# Revit family: QF_ELECTROLUXPROFESSIONAL_600673_EPBC1W2
name_source: partatom
category: Specialty Equipment
revit_build: Autodesk Revit 2018 (Build: 20190510_1515(x64)
units: mm (PartAtom-declared; Revit-internal decimal feet)

## family parameters
Always vertical = Yes
Cut with Voids When Loaded = No
Part Type = Normal
Room Calculation Point = No
Round Connector Dimension = Use Diameter
Shared = No
Work Plane-Based = No

## types (1)
- QF_ELECTROLUXPROFESSIONAL_600673_EPBC1W2
    Accessory = Yes
    Apparent Power = 0 VA
    Cold Water Connection Height = 126 mm
    Cold Water Flow = 0 GPM
    Cold Water Maximum Pressure = 0.00 psi
    Cold Water Minimum Pressure = 0.00 psi
    Cold Water RI Height = 0 mm  [stored 0 ft]
    Cold Water Size = 1"
    Cold Water Temperature Recommended = 0 °F
    Compressed Air Pressure = 0.00 psi
    Compressed Air Size = 0"
    Compressed Air Volume = 0 GPM
    Condensate Return Size = 0"
    Conn Conduit = Yes
    Cycle = 50 Hz
    Depth = 482 mm
    Depth Actual = 486 mm
    Description = PB WARMER SHUTTLE BREWER, SINGLE
    Direct Waste Size = 0"
    Elec Conn Connection Height = 0 mm  [stored 0 ft]
    Elec Conn RI Height = 227 mm
    FL Amps = 0 A
    Foodservice Equipment Identifier = Yes
    Gas Input Pressure = 0.0
    Gas KW = 0
    Gas Size = 0"
    HP = 3.8 HP
    Height = 761 mm
    Height Actual = 852 mm
    Hot Water Size = 0"
    Identify Quantity as Lot = Yes
    Item Number = 600673
    Length Actual = 232 mm  [stored 0.761155 ft]
    Manufacturer = Electrolux
    Max Overcurrent Protection = 0 A
    Min Ckt Ampacity = 0 A
    Model = EPBC1W2
    Number of Poles = 1
    Phase = 1
    Refrigerant Compressor Remote = Yes
    Refrigeration Liquid Line Size = 0"
    Refrigeration Suction Line Size = 0"
    Steam Pounds per Hour = 0
    Steam Supply Maximum Pressure = 0.00 psi
    Steam Supply Minimum Pressure = 0.00 psi
    Steam Supply Size = 0"
    URL = http://professional.electrolux.com
    URL Manufacturer = http://professional.electrolux.com
    Volts = 230 V
    Watts = 0 W
    Weight = 0.00 lbm
    Weight in Kilograms = 18
    Width = 229 mm

note: source unit labels omitted for Gas Input Pressure — the stored unit's dimension contradicts the parameter name (converter mislabeling)

note: [stored X ft] marks values corroborated as IEEE doubles in the binary element streams (Revit-internal decimal feet)

## geometry (parser evidence)
native form markers: Sweep x3
no freeform markers — native parametric forms only
